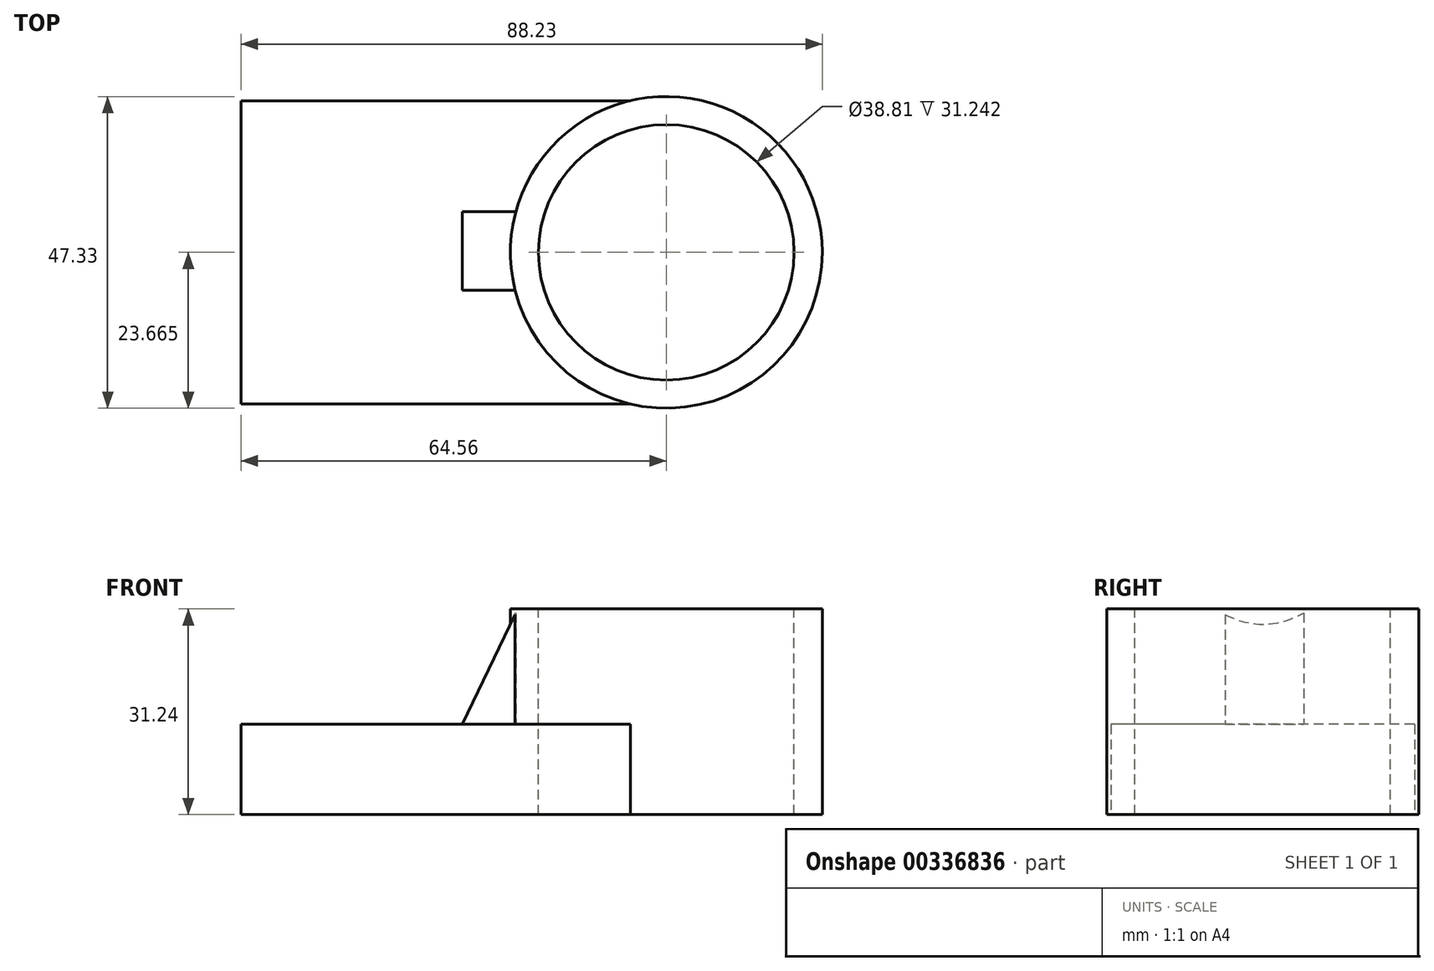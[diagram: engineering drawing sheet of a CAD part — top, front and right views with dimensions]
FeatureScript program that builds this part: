
annotation { "Feature Type Name" : "Feature", "Feature Type Description" : "" }
export const myFeature = defineFeature(function(context is Context, id is Id, definition is map)
    precondition{}
    {
        {
            var Q0;
            Q0=qCreatedBy(makeId("Top.planeOp"),FACE);
            var sketch = newSketch(context, id + "F0", { "sketchPlane" : qUnion([Q0])});
            skLineSegment(sketch, "E0.bottom", {"start": v(-52.35, 28.77) * mm, "end": v(12.2, 28.77) * mm});
            skLineSegment(sketch, "E0.top", {"start": v(-52.35, -17.3) * mm, "end": v(12.2, -17.3) * mm});
            skLineSegment(sketch, "E0.left", {"start": v(-52.35, 28.77) * mm, "end": v(-52.35, -17.3) * mm});
            skLineSegment(sketch, "E0.right", {"start": v(12.2, 28.77) * mm, "end": v(12.2, -17.3) * mm});
            skCircle(sketch, "E1", {"center": v(12.2, 5.73) * mm, "radius": 23.67 * mm});
            skSolve(sketch);
        }
        {
            var Q0;
            {var subQ0=sQuery(id+"F0.wireOp",EDGE,"E0.left");Q0=makeQuery(id+"F0.imprint","IMPRINT",FACE,{"disambiguationData":[TD([[makeQuery(id+"F0.imprint","IMPRINT",EDGE,{"derivedFrom":subQ0}),1.0]])]});}
            extrude(context, id + "F1", {"entities" : qUnion([Q0]), "depth" : 13.72 * mm});
        }
        {
            var Q0;
            {var subQ0=sQuery(id+"F0.wireOp",EDGE,"E0.right");Q0=makeQuery(id+"F0.imprint","IMPRINT",FACE,{"disambiguationData":[TD([[makeQuery(id+"F0.imprint","IMPRINT",EDGE,{"derivedFrom":subQ0}),1.0]])]});}
            var Q1;
            {var subQ0=sQuery(id+"F0.wireOp",EDGE,"E0.right");Q1=makeQuery(id+"F0.imprint","IMPRINT",FACE,{"disambiguationData":[TD([[makeQuery(id+"F0.imprint","IMPRINT",EDGE,{"derivedFrom":subQ0}),-1.0]])]});}
            extrude(context, id + "F2", {"entities" : qUnion([Q0, Q1]), "operationType" : NewBodyOperationType.ADD, "depth" : 31.24 * mm});
        }
        {
            var Q0;
            Q0=makeQuery(id+"F2.opExtrude","CAP_FACE",FACE,{"disambiguationData":[OSD([sQuery(id+"F0.wireOp",EDGE,"E1")])],"isStart":false});
            var sketch = newSketch(context, id + "F3", { "sketchPlane" : qUnion([Q0])});
            skCircle(sketch, "E2", {"center": v(12.2, 5.73) * mm, "radius": 19.4 * mm});
            skSolve(sketch);
        }
        {
            var Q0;
            Q0=makeQuery(id+"F3.imprint","IMPRINT",FACE,{"disambiguationData":[TD([[makeQuery(id+"F3.imprint","IMPRINT",EDGE,{"derivedFrom":sQuery(id+"F3.wireOp",EDGE,"E2")}),1.0]])]});
            extrude(context, id + "F4", {"entities" : qUnion([Q0]), "operationType" : NewBodyOperationType.REMOVE, "oppositeDirection" : true, "depth" : 44.45 * mm});
        }
        {
            var Q0;
            Q0=qCreatedBy(makeId("Front.planeOp"),FACE);
            var sketch = newSketch(context, id + "F5", { "sketchPlane" : qUnion([Q0])});
            skLineSegment(sketch, "E3", {"start": v(-10.57, 30.78) * mm, "end": v(-10.57, 13.29) * mm});
            skLineSegment(sketch, "E4", {"start": v(-10.57, 13.29) * mm, "end": v(-18.97, 13.29) * mm});
            skLineSegment(sketch, "E5", {"start": v(-18.97, 13.29) * mm, "end": v(-10.57, 30.78) * mm});
            skSolve(sketch);
        }
        {
            var Q0;
            Q0 = qSketchRegion(id + "F5", true);
            extrude(context, id + "F6", {"entities" : qUnion([Q0]), "operationType" : NewBodyOperationType.ADD, "oppositeDirection" : true, "depth" : 11.94 * mm});
        }
    });
